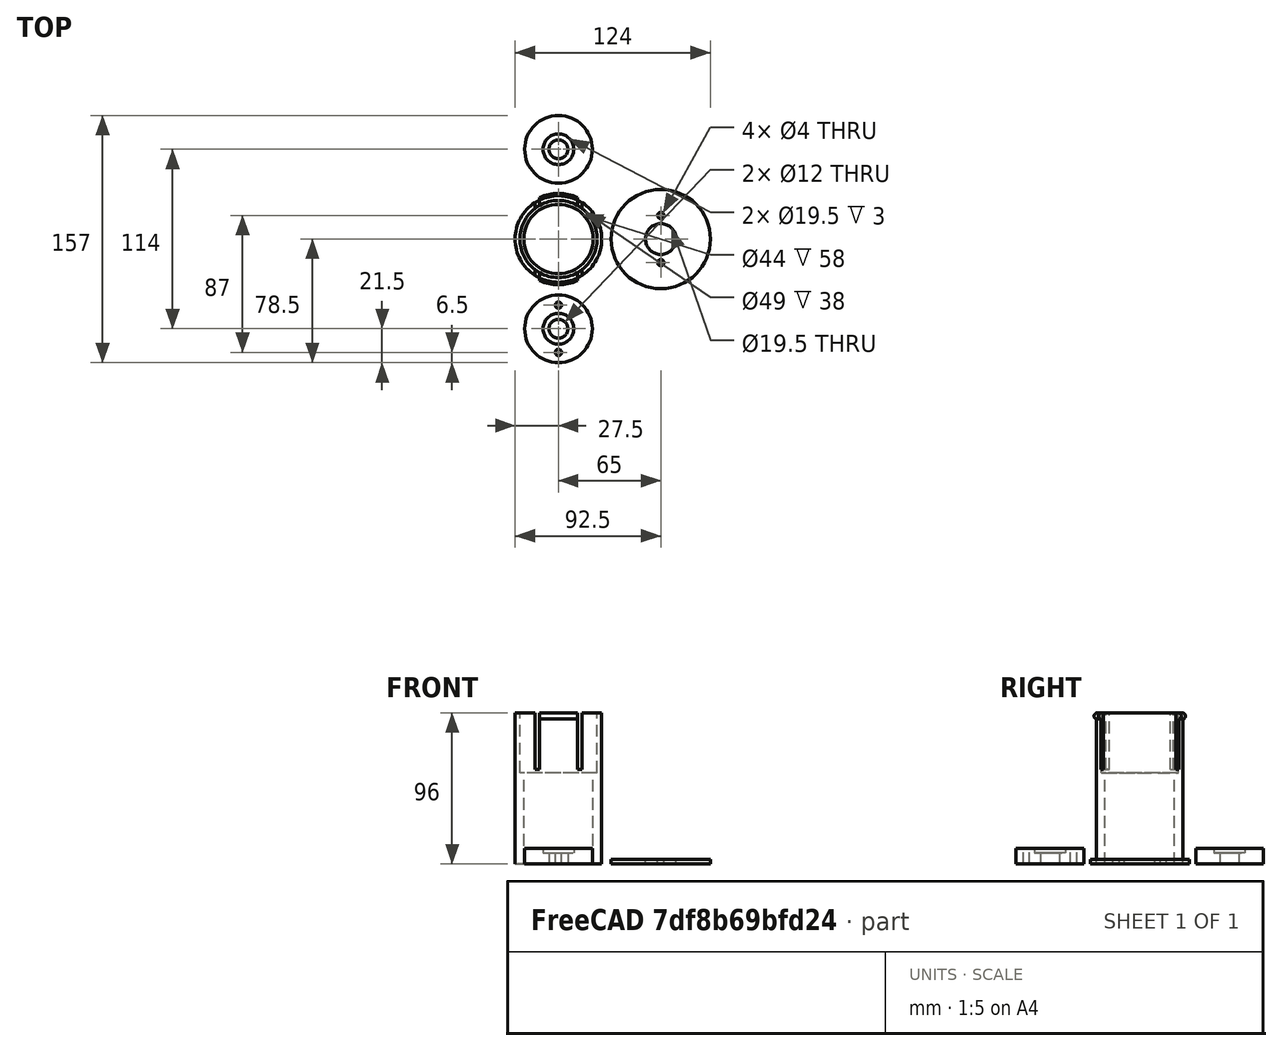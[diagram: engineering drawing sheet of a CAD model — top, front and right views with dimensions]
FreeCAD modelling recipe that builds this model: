
FCSTD DOCUMENT  (FreeCAD 0.14R3700 (Git))
Label: filament holder
License: CC-BY 3.0
LicenseURL: http://creativecommons.org/licenses/by/3.0/
objects: Part::Cylinder×14, Part::Cut×10, Part::MultiFuse×5, Part::Feature×4, Part::Torus×2, Part::Box×2
note: 37 computed .brp shape members not serialized (recipe doc carries the construction recipe); baked Part::Feature solids carry a one-line shape summary decoded from their .brp

FEATURE [Part::Cylinder] Cylinder
  Angle = 360
  Height = 96
  Radius = 27.5
FEATURE [Part::Cylinder] Cylinder001
  Angle = 360
  Height = 55
  Placement = pos=(0,0,58) rot=(0,0,1;0rad)
  Radius = 24.5
FEATURE [Part::Cylinder] Cylinder002
  Angle = 360
  Height = 60
  Placement = pos=(0,0,58) rot=(0,0,1;0rad)
  Radius = 24.5
FEATURE [Part::Cylinder] Cylinder003
  Angle = 360
  Height = 10
  Placement = pos=(0,0,3) rot=(0,0,1;0rad)
  Radius = 21.5
FEATURE [Part::Cylinder] Cylinder004
  Angle = 360
  Height = 3
  Radius = 31.5
FEATURE [Part::Cylinder] Cylinder005
  Angle = 360
  Height = 20
  Radius = 6
FEATURE [Part::Cylinder] Cylinder006
  Angle = 360
  Height = 6
  Radius = 9.75
FEATURE [Part::Cylinder] Cylinder007
  Angle = 360
  Height = 6
  Radius = 9.75
FEATURE [Part::Cut] Cut001  label="end flange"
  Base = -> Cylinder004
  Tool = -> Cylinder006
FEATURE [Part::Cut] Cut002
  Base = -> Cylinder003
  Tool = -> Cylinder007
FEATURE [Part::Cut] Cut003  label="large bearing ring"
  Base = -> Cut002
  Placement = pos=(0,57,13) rot=(0,1,0;3.14159rad)
  Tool = -> Cylinder005
FEATURE [Part::Cylinder] Cylinder008
  Angle = 360
  Height = 90
  Radius = 22
FEATURE [Part::Cut] Cut
  Base = -> Cylinder
  Tool = -> Cylinder008
FEATURE [Part::MultiFuse] Fusion
  Shapes = -> [Cylinder002,Cylinder001]
FEATURE [Part::Cut] Cut004
  Base = -> Cut
  Tool = -> Fusion
FEATURE [Part::Cylinder] Cylinder009
  Angle = 360
  Height = 20
  Radius = 6
FEATURE [Part::Cut] Cut006
  Base = -> Cylinder003
  Tool = -> Cylinder007
FEATURE [Part::Cut] Cut005  label="small bearing ring"
  Base = -> Cut006
  Placement = pos=(0,0,13) rot=(0,1,0;3.14159rad)
  Tool = -> Cylinder009
FEATURE [Part::Torus] Torus
  Angle1 = -180
  Angle2 = 180
  Angle3 = 60
  Placement = pos=(0,0,94) rot=(0,0,1;1.0472rad)
  Radius1 = 27
  Radius2 = 2
FEATURE [Part::Torus] Torus001
  Angle1 = -180
  Angle2 = 180
  Angle3 = 60
  Placement = pos=(0,0,94) rot=(0,0,1;4.18879rad)
  Radius1 = 27
  Radius2 = 2
FEATURE [Part::Box] Box  label="Cube"
  Height = 40
  Length = 3
  Placement = pos=(12,-40,60) rot=(0,0,1;0rad)
  Width = 90
FEATURE [Part::Box] Box001  label="Cube001"
  Height = 40
  Length = 3
  Placement = pos=(-15,-40,60) rot=(0,0,1;0rad)
  Width = 90
FEATURE [Part::MultiFuse] Fusion001
  Shapes = -> [Cut004,Torus,Torus001]
FEATURE [Part::MultiFuse] Fusion002
  Shapes = -> [Box001,Box]
FEATURE [Part::Cut] Cut007  label="main bit"
  Base = -> Fusion001
  Tool = -> Fusion002
FEATURE [Part::Cylinder] Cylinder010
  Angle = 360
  Height = 15
  Placement = pos=(0,15,-1) rot=(0,0,1;0rad)
  Radius = 2
FEATURE [Part::Cylinder] Cylinder011
  Angle = 360
  Height = 15
  Placement = pos=(0,-15,-1) rot=(0,0,1;0.017453rad)
  Radius = 2
FEATURE [Part::Cylinder] Cylinder012
  Angle = 360
  Height = 15
  Placement = pos=(0,-15,-1) rot=(0,0,1;0.017453rad)
  Radius = 2
FEATURE [Part::Cylinder] Cylinder013
  Angle = 360
  Height = 15
  Placement = pos=(0,15,-1) rot=(0,0,1;0rad)
  Radius = 2
FEATURE [Part::MultiFuse] Fusion003
  Shapes = -> [Cylinder011,Cylinder010]
FEATURE [Part::MultiFuse] Fusion004
  Shapes = -> [Cylinder013,Cylinder012]
FEATURE [Part::Cut] Cut008  label="small bearing ring001"
  Base = -> Cut005
  Placement = pos=(0,-57,0) rot=(0,0,1;0rad)
  Tool = -> Fusion003
FEATURE [Part::Cut] Cut009  label="end flange001"
  Base = -> Cut001
  Placement = pos=(65,0,0) rot=(0,0,1;0rad)
  Tool = -> Fusion004
FEATURE [Part::Feature] Cut003_solid  label="large bearing ring (Solid)"
  shape: bbox 43 x 43 x 10 mm, 6 faces (baked)
FEATURE [Part::Feature] Cut007_solid  label="main bit (Solid)"
  shape: bbox 55 x 60.64 x 96 mm, 29 faces (baked)
FEATURE [Part::Feature] Cut008_solid  label="small bearing ring001 (Solid)"
  shape: bbox 43 x 43 x 10 mm, 8 faces (baked)
FEATURE [Part::Feature] Cut009_solid  label="end flange001 (Solid)"
  shape: bbox 63 x 63 x 3 mm, 6 faces (baked)
